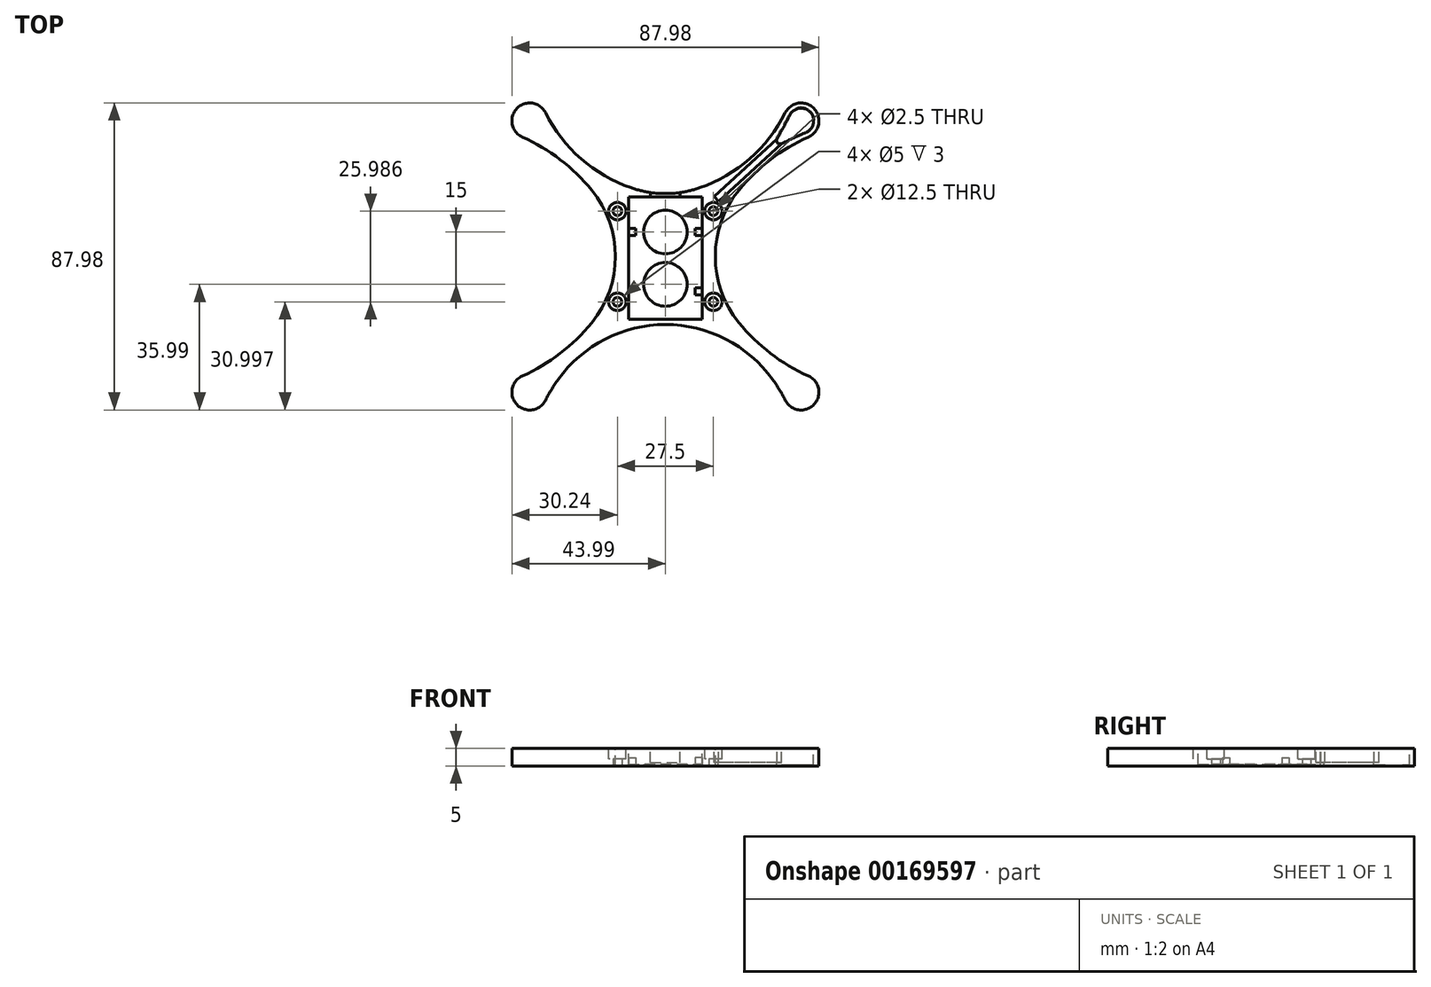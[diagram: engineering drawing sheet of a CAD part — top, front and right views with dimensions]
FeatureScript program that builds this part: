
annotation { "Feature Type Name" : "Feature", "Feature Type Description" : "" }
export const myFeature = defineFeature(function(context is Context, id is Id, definition is map)
    precondition{}
    {
        {
            var Q0;
            Q0=qCreatedBy(makeId("Top.planeOp"),FACE);
            var sketch = newSketch(context, id + "F0", { "sketchPlane" : qUnion([Q0])});
            skLineSegment(sketch, "E0.bottom", {"start": v(50, 50) * mm, "end": v(-50, 50) * mm, "construction": true});
            skLineSegment(sketch, "E0.top", {"start": v(50, -50) * mm, "end": v(-50, -50) * mm, "construction": true});
            skLineSegment(sketch, "E0.left", {"start": v(50, 50) * mm, "end": v(50, -50) * mm, "construction": true});
            skLineSegment(sketch, "E0.right", {"start": v(-50, 50) * mm, "end": v(-50, -50) * mm, "construction": true});
            skPoint(sketch, "E0.middle", {"position": v(0, 0) * mm});
            skSolve(sketch);
        }
        {
            var Q0;
            Q0=qCreatedBy(makeId("Top.planeOp"),FACE);
            var sketch = newSketch(context, id + "F1", { "sketchPlane" : qUnion([Q0])});
            skCircle(sketch, "E1", {"center": v(38.9, 38.9) * mm, "radius": 3.6 * mm, "construction": true});
            skLineSegment(sketch, "E2", {"start": v(0, 0) * mm, "end": v(65.42, 0) * mm, "construction": true});
            skLineSegment(sketch, "E3", {"start": v(0, 0) * mm, "end": v(0, 57) * mm, "construction": true});
            skLineSegment(sketch, "E4.bottom", {"start": v(11, 17.5) * mm, "end": v(-11, 17.5) * mm, "construction": true});
            skLineSegment(sketch, "E4.top", {"start": v(11, -17.5) * mm, "end": v(-11, -17.5) * mm, "construction": true});
            skLineSegment(sketch, "E4.left", {"start": v(11, 17.5) * mm, "end": v(11, -17.5) * mm, "construction": true});
            skLineSegment(sketch, "E4.right", {"start": v(-11, 17.5) * mm, "end": v(-11, -17.5) * mm, "construction": true});
            skPoint(sketch, "E4.middle", {"position": v(0, 0) * mm});
            skArc(sketch, "E5", {"start": v(40.98, 34.24) * mm, "mid": v(42.57, 42.42) * mm, "end": v(34.33, 41.17) * mm});
            skLineSegment(sketch, "E6", {"start": v(11, 17.5) * mm, "end": v(38.9, 38.9) * mm, "construction": true});
            skArc(sketch, "E7", {"start": v(40.98, 34.24) * mm, "mid": v(22.26, 20.39) * mm, "end": v(11, 0) * mm});
            skArc(sketch, "E8", {"start": v(0, 17.5) * mm, "mid": v(20.2, 24.92) * mm, "end": v(34.33, 41.17) * mm});
            skArc(sketch, "E9.MirrorCS", {"start": v(-40.98, 34.24) * mm, "mid": v(-42.57, 42.42) * mm, "end": v(-34.33, 41.17) * mm});
            skArc(sketch, "E10.MirrorCS", {"start": v(0, 17.5) * mm, "mid": v(-20.2, 24.92) * mm, "end": v(-34.33, 41.17) * mm});
            skArc(sketch, "E11.MirrorCS", {"start": v(-40.98, 34.24) * mm, "mid": v(-22.26, 20.39) * mm, "end": v(-11, 0) * mm});
            skArc(sketch, "E12.MirrorCS", {"start": v(40.98, -34.24) * mm, "mid": v(42.57, -42.42) * mm, "end": v(34.33, -41.17) * mm});
            skArc(sketch, "E13.MirrorCS", {"start": v(30.74, -35.24) * mm, "mid": v(32.66, -38.14) * mm, "end": v(34.33, -41.17) * mm});
            skArc(sketch, "E14.MirrorCS", {"start": v(40.98, -34.24) * mm, "mid": v(22.26, -20.39) * mm, "end": v(11, 0) * mm});
            skArc(sketch, "E15.MirrorCS", {"start": v(-40.98, -34.24) * mm, "mid": v(-42.57, -42.42) * mm, "end": v(-34.33, -41.17) * mm});
            skArc(sketch, "E16.MirrorCS", {"start": v(-30.74, -35.24) * mm, "mid": v(-32.66, -38.14) * mm, "end": v(-34.33, -41.17) * mm});
            skArc(sketch, "E17.MirrorCS", {"start": v(-40.98, -34.24) * mm, "mid": v(-22.26, -20.39) * mm, "end": v(-11, 0) * mm});
            skLineSegment(sketch, "E18", {"start": v(0, 0) * mm, "end": v(50, 50) * mm, "construction": true});
            skArc(sketch, "E19", {"start": v(30.74, -35.24) * mm, "mid": v(0, -19.5) * mm, "end": v(-30.74, -35.24) * mm});
            skPoint(sketch, "E20.orphan", {"position": v(0, -17.5) * mm});
            skSolve(sketch);
        }
        {
            var Q0;
            Q0=makeQuery(id+"F1.imprint","IMPRINT",FACE,{"disambiguationData":[TD([[makeQuery(id+"F1.imprint","IMPRINT",EDGE,{"derivedFrom":sQuery(id+"F1.wireOp",EDGE,"E5")}),1.0]])]});
            extrude(context, id + "F2", {"entities" : qUnion([Q0]), "depth" : 5 * mm});
        }
        {
            var Q0;
            Q0=makeQuery(id+"F2.opExtrude","CAP_FACE",FACE,{"disambiguationData":[OSD([sQuery(id+"F1.wireOp",EDGE,"E5"),sQuery(id+"F1.wireOp",EDGE,"E7"),sQuery(id+"F1.wireOp",EDGE,"E8"),sQuery(id+"F1.wireOp",EDGE,"E9.MirrorCS"),sQuery(id+"F1.wireOp",EDGE,"E10.MirrorCS"),sQuery(id+"F1.wireOp",EDGE,"E11.MirrorCS"),sQuery(id+"F1.wireOp",EDGE,"E12.MirrorCS"),sQuery(id+"F1.wireOp",EDGE,"E13.MirrorCS"),sQuery(id+"F1.wireOp",EDGE,"E14.MirrorCS"),sQuery(id+"F1.wireOp",EDGE,"E15.MirrorCS"),sQuery(id+"F1.wireOp",EDGE,"E16.MirrorCS"),sQuery(id+"F1.wireOp",EDGE,"E17.MirrorCS")])],"isStart":false});
            var sketch = newSketch(context, id + "F3", { "sketchPlane" : qUnion([Q0])});
            skArc(sketch, "E21", {"start": v(40.33, 35.6) * mm, "mid": v(41.51, 41.36) * mm, "end": v(35.69, 40.53) * mm});
            skArc(sketch, "E22", {"start": v(32.02, 33.75) * mm, "mid": v(32.16, 32.57) * mm, "end": v(33.33, 32.35) * mm});
            skArc(sketch, "E23", {"start": v(40.33, 35.6) * mm, "mid": v(36.81, 34.01) * mm, "end": v(33.33, 32.35) * mm});
            skLineSegment(sketch, "E24", {"start": v(32.89, 33.25) * mm, "end": v(38.9, 38.9) * mm, "construction": true});
            skArc(sketch, "E25.MirrorCS", {"start": v(35.69, 40.53) * mm, "mid": v(33.9, 37.12) * mm, "end": v(32.02, 33.75) * mm});
            skLineSegment(sketch, "E26", {"start": v(27.7, 25.78) * mm, "end": v(24.94, 28.7) * mm});
            skSolve(sketch);
        }
        {
            var Q0;
            Q0=makeQuery(id+"F3.imprint","IMPRINT",FACE,{"disambiguationData":[TD([[makeQuery(id+"F3.imprint","IMPRINT",EDGE,{"derivedFrom":sQuery(id+"F3.wireOp",EDGE,"E21")}),1.0]])]});
            extrude(context, id + "F4", {"entities" : qUnion([Q0]), "operationType" : NewBodyOperationType.REMOVE, "endBound" : BoundingType.THROUGH_ALL, "oppositeDirection" : true, "depth" : 25 * mm});
        }
        {
            var Q0;
            Q0=makeQuery(id+"F2.opExtrude","CAP_FACE",FACE,{"disambiguationData":[OSD([sQuery(id+"F1.wireOp",EDGE,"E5"),sQuery(id+"F1.wireOp",EDGE,"E7"),sQuery(id+"F1.wireOp",EDGE,"E8"),sQuery(id+"F1.wireOp",EDGE,"E9.MirrorCS"),sQuery(id+"F1.wireOp",EDGE,"E10.MirrorCS"),sQuery(id+"F1.wireOp",EDGE,"E11.MirrorCS"),sQuery(id+"F1.wireOp",EDGE,"E12.MirrorCS"),sQuery(id+"F1.wireOp",EDGE,"E13.MirrorCS"),sQuery(id+"F1.wireOp",EDGE,"E14.MirrorCS"),sQuery(id+"F1.wireOp",EDGE,"E15.MirrorCS"),sQuery(id+"F1.wireOp",EDGE,"E16.MirrorCS"),sQuery(id+"F1.wireOp",EDGE,"E17.MirrorCS"),sQuery(id+"F1.wireOp",EDGE,"E19")])],"isStart":false});
            var sketch = newSketch(context, id + "F5", { "sketchPlane" : qUnion([Q0])});
            skLineSegment(sketch, "E27", {"start": v(33.33, 32.35) * mm, "end": v(15.3, 15.76) * mm});
            skLineSegment(sketch, "E28", {"start": v(32.02, 33.75) * mm, "end": v(14, 17.17) * mm});
            skLineSegment(sketch, "E29", {"start": v(15.3, 15.76) * mm, "end": v(14, 17.17) * mm});
            skLineSegment(sketch, "E30", {"start": v(32.02, 33.75) * mm, "end": v(33.33, 32.35) * mm});
            skSolve(sketch);
        }
        {
            var Q0;
            Q0=makeQuery(id+"F5.imprint","IMPRINT",FACE,{"disambiguationData":[TD([[makeQuery(id+"F5.imprint","IMPRINT",EDGE,{"derivedFrom":sQuery(id+"F5.wireOp",EDGE,"E27")}),-1.0]])]});
            extrude(context, id + "F6", {"entities" : qUnion([Q0]), "operationType" : NewBodyOperationType.REMOVE, "oppositeDirection" : true, "depth" : 4 * mm});
        }
        {
            var Q0;
            Q0=makeQuery(id+"F2.opExtrude","SWEPT_EDGE",EDGE,{"disambiguationData":[OSD([sQuery(id+"F1.wireOp",EDGE,"E7"),sQuery(id+"F1.wireOp",EDGE,"E14.MirrorCS")])]});
            var Q1;
            Q1=makeQuery(id+"F2.opExtrude","SWEPT_EDGE",EDGE,{"disambiguationData":[OSD([sQuery(id+"F1.wireOp",EDGE,"E13.MirrorCS"),sQuery(id+"F1.wireOp",EDGE,"E16.MirrorCS")])]});
            var Q2;
            Q2=makeQuery(id+"F2.opExtrude","SWEPT_EDGE",EDGE,{"disambiguationData":[OSD([sQuery(id+"F1.wireOp",EDGE,"E11.MirrorCS"),sQuery(id+"F1.wireOp",EDGE,"E17.MirrorCS")])]});
            var Q3;
            Q3=makeQuery(id+"F2.opExtrude","SWEPT_EDGE",EDGE,{"disambiguationData":[OSD([sQuery(id+"F1.wireOp",EDGE,"E8"),sQuery(id+"F1.wireOp",EDGE,"E10.MirrorCS")])]});
            fillet(context, id + "F7", {"entities" : qUnion([Q0, Q1, Q2, Q3]), "radius" : 30 * mm, "tangentPropagation" : true, "allowEdgeOverflow" : false});
        }
        {
            var Q0;
            Q0=makeQuery(id+"F4.boolean.opBoolean","INTERSECT",EDGE,{"derivedFrom":[makeQuery(id+"F2.opExtrude","CAP_FACE",FACE,{"disambiguationData":[OSD([sQuery(id+"F1.wireOp",EDGE,"E5"),sQuery(id+"F1.wireOp",EDGE,"E7"),sQuery(id+"F1.wireOp",EDGE,"E8"),sQuery(id+"F1.wireOp",EDGE,"E9.MirrorCS"),sQuery(id+"F1.wireOp",EDGE,"E10.MirrorCS"),sQuery(id+"F1.wireOp",EDGE,"E11.MirrorCS"),sQuery(id+"F1.wireOp",EDGE,"E12.MirrorCS"),sQuery(id+"F1.wireOp",EDGE,"E13.MirrorCS"),sQuery(id+"F1.wireOp",EDGE,"E14.MirrorCS"),sQuery(id+"F1.wireOp",EDGE,"E15.MirrorCS"),sQuery(id+"F1.wireOp",EDGE,"E16.MirrorCS"),sQuery(id+"F1.wireOp",EDGE,"E17.MirrorCS")])],"isStart":true}),makeQuery(id+"F4.opExtrude","SWEPT_FACE",FACE,{"disambiguationData":[OSD([sQuery(id+"F3.wireOp",EDGE,"E21")])]})]});
            var Q1;
            Q1=makeQuery(id+"FYeeliCWMMzlBYI_1.1.F4.boolean.opBoolean","INTERSECT",EDGE,{"derivedFrom":[makeQuery(id+"F2.opExtrude","CAP_FACE",FACE,{"disambiguationData":[OSD([sQuery(id+"F1.wireOp",EDGE,"E5"),sQuery(id+"F1.wireOp",EDGE,"E7"),sQuery(id+"F1.wireOp",EDGE,"E8"),sQuery(id+"F1.wireOp",EDGE,"E9.MirrorCS"),sQuery(id+"F1.wireOp",EDGE,"E10.MirrorCS"),sQuery(id+"F1.wireOp",EDGE,"E11.MirrorCS"),sQuery(id+"F1.wireOp",EDGE,"E12.MirrorCS"),sQuery(id+"F1.wireOp",EDGE,"E13.MirrorCS"),sQuery(id+"F1.wireOp",EDGE,"E14.MirrorCS"),sQuery(id+"F1.wireOp",EDGE,"E15.MirrorCS"),sQuery(id+"F1.wireOp",EDGE,"E16.MirrorCS"),sQuery(id+"F1.wireOp",EDGE,"E17.MirrorCS")])],"isStart":true}),makeQuery(id+"FYeeliCWMMzlBYI_1.1.F4.opExtrude","SWEPT_FACE",FACE,{"disambiguationData":[OSD([sQuery(id+"F3.wireOp",EDGE,"E21")])]})]});
            var Q2;
            Q2=makeQuery(id+"FTFssc0xpSEtFVF_1.1.FYeeliCWMMzlBYI_1.1.F4.boolean.opBoolean","INTERSECT",EDGE,{"derivedFrom":[makeQuery(id+"F2.opExtrude","CAP_FACE",FACE,{"disambiguationData":[OSD([sQuery(id+"F1.wireOp",EDGE,"E5"),sQuery(id+"F1.wireOp",EDGE,"E7"),sQuery(id+"F1.wireOp",EDGE,"E8"),sQuery(id+"F1.wireOp",EDGE,"E9.MirrorCS"),sQuery(id+"F1.wireOp",EDGE,"E10.MirrorCS"),sQuery(id+"F1.wireOp",EDGE,"E11.MirrorCS"),sQuery(id+"F1.wireOp",EDGE,"E12.MirrorCS"),sQuery(id+"F1.wireOp",EDGE,"E13.MirrorCS"),sQuery(id+"F1.wireOp",EDGE,"E14.MirrorCS"),sQuery(id+"F1.wireOp",EDGE,"E15.MirrorCS"),sQuery(id+"F1.wireOp",EDGE,"E16.MirrorCS"),sQuery(id+"F1.wireOp",EDGE,"E17.MirrorCS")])],"isStart":true}),makeQuery(id+"FTFssc0xpSEtFVF_1.1.FYeeliCWMMzlBYI_1.1.F4.opExtrude","SWEPT_FACE",FACE,{"disambiguationData":[OSD([sQuery(id+"F3.wireOp",EDGE,"E21")])]})]});
            var Q3;
            Q3=makeQuery(id+"FTFssc0xpSEtFVF_1.1.F4.boolean.opBoolean","INTERSECT",EDGE,{"derivedFrom":[makeQuery(id+"F2.opExtrude","CAP_FACE",FACE,{"disambiguationData":[OSD([sQuery(id+"F1.wireOp",EDGE,"E5"),sQuery(id+"F1.wireOp",EDGE,"E7"),sQuery(id+"F1.wireOp",EDGE,"E8"),sQuery(id+"F1.wireOp",EDGE,"E9.MirrorCS"),sQuery(id+"F1.wireOp",EDGE,"E10.MirrorCS"),sQuery(id+"F1.wireOp",EDGE,"E11.MirrorCS"),sQuery(id+"F1.wireOp",EDGE,"E12.MirrorCS"),sQuery(id+"F1.wireOp",EDGE,"E13.MirrorCS"),sQuery(id+"F1.wireOp",EDGE,"E14.MirrorCS"),sQuery(id+"F1.wireOp",EDGE,"E15.MirrorCS"),sQuery(id+"F1.wireOp",EDGE,"E16.MirrorCS"),sQuery(id+"F1.wireOp",EDGE,"E17.MirrorCS")])],"isStart":true}),makeQuery(id+"FTFssc0xpSEtFVF_1.1.F4.opExtrude","SWEPT_FACE",FACE,{"disambiguationData":[OSD([sQuery(id+"F3.wireOp",EDGE,"6V2njJEu-L4nl-PxpZ-iP1S-ceyWdav9gjuh")])]})]});
            chamfer(context, id + "F8", {"entities" : qUnion([Q0, Q1, Q2, Q3]), "width" : .3 * mm, "tangentPropagation" : true});
        }
        {
            var Q0;
            Q0=makeQuery(id+"F2.opExtrude","CAP_FACE",FACE,{"disambiguationData":[OSD([sQuery(id+"F1.wireOp",EDGE,"E5"),sQuery(id+"F1.wireOp",EDGE,"E7"),sQuery(id+"F1.wireOp",EDGE,"E8"),sQuery(id+"F1.wireOp",EDGE,"E9.MirrorCS"),sQuery(id+"F1.wireOp",EDGE,"E10.MirrorCS"),sQuery(id+"F1.wireOp",EDGE,"E11.MirrorCS"),sQuery(id+"F1.wireOp",EDGE,"E12.MirrorCS"),sQuery(id+"F1.wireOp",EDGE,"E13.MirrorCS"),sQuery(id+"F1.wireOp",EDGE,"E14.MirrorCS"),sQuery(id+"F1.wireOp",EDGE,"E15.MirrorCS"),sQuery(id+"F1.wireOp",EDGE,"E16.MirrorCS"),sQuery(id+"F1.wireOp",EDGE,"E17.MirrorCS")])],"isStart":false});
            var sketch = newSketch(context, id + "F9", { "sketchPlane" : qUnion([Q0])});
            skLineSegment(sketch, "E31.bottom", {"start": v(-10.5, -18) * mm, "end": v(10.5, -18) * mm});
            skLineSegment(sketch, "E31.top", {"start": v(-10.5, 17) * mm, "end": v(10.5, 17) * mm});
            skLineSegment(sketch, "E31.left", {"start": v(-10.5, -18) * mm, "end": v(-10.5, 17) * mm});
            skLineSegment(sketch, "E31.right", {"start": v(10.5, -18) * mm, "end": v(10.5, 17) * mm});
            skSolve(sketch);
        }
        {
            var Q0;
            Q0 = qSketchRegion(id + "F9", true);
            extrude(context, id + "F10", {"entities" : qUnion([Q0]), "operationType" : NewBodyOperationType.REMOVE, "oppositeDirection" : true, "depth" : 4.5 * mm});
        }
        {
            var Q0;
            Q0=makeQuery(id+"F10.boolean.opBoolean","COPY",FACE,{"derivedFrom":makeQuery(id+"F10.opExtrude","CAP_FACE",FACE,{"disambiguationData":[OSD([sQuery(id+"F9.wireOp",EDGE,"E31.bottom"),sQuery(id+"F9.wireOp",EDGE,"E31.top"),sQuery(id+"F9.wireOp",EDGE,"E31.left"),sQuery(id+"F9.wireOp",EDGE,"E31.right")])],"isStart":false})});
            var sketch = newSketch(context, id + "F11", { "sketchPlane" : qUnion([Q0])});
            skLineSegment(sketch, "E32.bottom", {"start": v(-10.5, 6) * mm, "end": v(-8.5, 6) * mm});
            skLineSegment(sketch, "E32.top", {"start": v(-10.5, 8) * mm, "end": v(-8.5, 8) * mm});
            skLineSegment(sketch, "E32.left", {"start": v(-10.5, 8) * mm, "end": v(-10.5, 6) * mm});
            skLineSegment(sketch, "E32.right", {"start": v(-8.5, 8) * mm, "end": v(-8.5, 6) * mm});
            skLineSegment(sketch, "E33.MirrorCS", {"start": v(10.5, 6) * mm, "end": v(8.5, 6) * mm});
            skLineSegment(sketch, "E34.MirrorCS", {"start": v(8.5, 8) * mm, "end": v(8.5, 6) * mm});
            skLineSegment(sketch, "E35.MirrorCS", {"start": v(10.5, 8) * mm, "end": v(8.5, 8) * mm});
            skLineSegment(sketch, "E36.MirrorCS", {"start": v(10.5, 8) * mm, "end": v(10.5, 6) * mm});
            skLineSegment(sketch, "E37.bottom", {"start": v(10.5, -11) * mm, "end": v(8.5, -11) * mm});
            skLineSegment(sketch, "E37.top", {"start": v(10.5, -9) * mm, "end": v(8.5, -9) * mm});
            skLineSegment(sketch, "E37.left", {"start": v(10.5, -11) * mm, "end": v(10.5, -9) * mm});
            skLineSegment(sketch, "E37.right", {"start": v(8.5, -11) * mm, "end": v(8.5, -9) * mm});
            skSolve(sketch);
        }
        {
            var Q0;
            Q0 = qSketchRegion(id + "F11", true);
            extrude(context, id + "F12", {"entities" : qUnion([Q0]), "operationType" : NewBodyOperationType.ADD, "depth" : 1.95 * mm});
        }
        {
            var Q0;
            Q0=qCreatedBy(makeId("Top.planeOp"),FACE);
            var sketch = newSketch(context, id + "F13", { "sketchPlane" : qUnion([Q0])});
            skCircle(sketch, "E38", {"center": v(-13.75, 13) * mm, "radius": 1.25 * mm});
            skCircle(sketch, "E39.MirrorC", {"center": v(13.75, 13) * mm, "radius": 1.25 * mm});
            skCircle(sketch, "E40.MirrorC", {"center": v(13.75, -13) * mm, "radius": 1.25 * mm});
            skCircle(sketch, "E41.MirrorC", {"center": v(-13.75, -13) * mm, "radius": 1.25 * mm});
            skCircle(sketch, "E42", {"center": v(0, 7) * mm, "radius": 6.25 * mm});
            skCircle(sketch, "E43", {"center": v(0, -8) * mm, "radius": 6.25 * mm});
            skSolve(sketch);
        }
        {
            var Q0;
            Q0 = qSketchRegion(id + "F13", true);
            extrude(context, id + "F14", {"entities" : qUnion([Q0]), "operationType" : NewBodyOperationType.REMOVE, "endBound" : BoundingType.THROUGH_ALL, "depth" : 25 * mm});
        }
        {
            var Q0;
            Q0=makeQuery(id+"F2.opExtrude","CAP_FACE",FACE,{"disambiguationData":[OSD([sQuery(id+"F1.wireOp",EDGE,"E5"),sQuery(id+"F1.wireOp",EDGE,"E7"),sQuery(id+"F1.wireOp",EDGE,"E8"),sQuery(id+"F1.wireOp",EDGE,"E9.MirrorCS"),sQuery(id+"F1.wireOp",EDGE,"E10.MirrorCS"),sQuery(id+"F1.wireOp",EDGE,"E11.MirrorCS"),sQuery(id+"F1.wireOp",EDGE,"E12.MirrorCS"),sQuery(id+"F1.wireOp",EDGE,"E13.MirrorCS"),sQuery(id+"F1.wireOp",EDGE,"E14.MirrorCS"),sQuery(id+"F1.wireOp",EDGE,"E15.MirrorCS"),sQuery(id+"F1.wireOp",EDGE,"E16.MirrorCS"),sQuery(id+"F1.wireOp",EDGE,"E17.MirrorCS"),sQuery(id+"F1.wireOp",EDGE,"E19")])],"isStart":false});
            var sketch = newSketch(context, id + "F15", { "sketchPlane" : qUnion([Q0])});
            skLineSegment(sketch, "E44.bottom", {"start": v(-4.25, 17) * mm, "end": v(4.25, 17) * mm});
            skLineSegment(sketch, "E44.top", {"start": v(-4.25, 22) * mm, "end": v(4.25, 22) * mm});
            skLineSegment(sketch, "E44.left", {"start": v(-4.25, 17) * mm, "end": v(-4.25, 22) * mm});
            skLineSegment(sketch, "E44.right", {"start": v(4.25, 17) * mm, "end": v(4.25, 22) * mm});
            skSolve(sketch);
        }
        {
            var Q0;
            {var subQ0=sQuery(id+"F15.wireOp",EDGE,"E44.top");Q0=makeQuery(id+"F15.imprint","IMPRINT",FACE,{"disambiguationData":[TD([[makeQuery(id+"F15.imprint","IMPRINT",EDGE,{"derivedFrom":subQ0}),-1.0]])]});}
            var Q1;
            {var subQ0=sQuery(id+"F15.wireOp",EDGE,"E44.bottom");Q1=makeQuery(id+"F15.imprint","IMPRINT",FACE,{"disambiguationData":[TD([[makeQuery(id+"F15.imprint","IMPRINT",EDGE,{"derivedFrom":subQ0}),1.0]])]});}
            extrude(context, id + "F16", {"entities" : qUnion([Q0, Q1]), "operationType" : NewBodyOperationType.REMOVE, "oppositeDirection" : true, "depth" : 4 * mm});
        }
        {
            var Q0;
            Q0=makeQuery(id+"F2.opExtrude","CAP_FACE",FACE,{"disambiguationData":[OSD([sQuery(id+"F1.wireOp",EDGE,"E5"),sQuery(id+"F1.wireOp",EDGE,"E7"),sQuery(id+"F1.wireOp",EDGE,"E8"),sQuery(id+"F1.wireOp",EDGE,"E9.MirrorCS"),sQuery(id+"F1.wireOp",EDGE,"E10.MirrorCS"),sQuery(id+"F1.wireOp",EDGE,"E11.MirrorCS"),sQuery(id+"F1.wireOp",EDGE,"E12.MirrorCS"),sQuery(id+"F1.wireOp",EDGE,"E13.MirrorCS"),sQuery(id+"F1.wireOp",EDGE,"E14.MirrorCS"),sQuery(id+"F1.wireOp",EDGE,"E15.MirrorCS"),sQuery(id+"F1.wireOp",EDGE,"E16.MirrorCS"),sQuery(id+"F1.wireOp",EDGE,"E17.MirrorCS"),sQuery(id+"F1.wireOp",EDGE,"E19")])],"isStart":false});
            var sketch = newSketch(context, id + "F17", { "sketchPlane" : qUnion([Q0])});
            skCircle(sketch, "E45", {"center": v(13.75, -13) * mm, "radius": 2.5 * mm});
            skCircle(sketch, "E46", {"center": v(-13.75, -13) * mm, "radius": 2.5 * mm});
            skCircle(sketch, "E47", {"center": v(-13.75, 13) * mm, "radius": 2.5 * mm});
            skCircle(sketch, "E48", {"center": v(13.75, 13) * mm, "radius": 2.5 * mm});
            skSolve(sketch);
        }
        {
            var Q0;
            Q0=makeQuery(id+"F17.imprint","IMPRINT",FACE,{"disambiguationData":[TD([[makeQuery(id+"F17.imprint","IMPRINT",EDGE,{"derivedFrom":sQuery(id+"F17.wireOp",EDGE,"E45")}),1.0]])]});
            var Q1;
            Q1=makeQuery(id+"F17.imprint","IMPRINT",FACE,{"disambiguationData":[TD([[makeQuery(id+"F17.imprint","IMPRINT",EDGE,{"derivedFrom":sQuery(id+"F17.wireOp",EDGE,"E46")}),1.0]])]});
            var Q2;
            Q2=makeQuery(id+"F17.imprint","IMPRINT",FACE,{"disambiguationData":[TD([[makeQuery(id+"F17.imprint","IMPRINT",EDGE,{"derivedFrom":sQuery(id+"F17.wireOp",EDGE,"E48")}),1.0]])]});
            var Q3;
            Q3=makeQuery(id+"F17.imprint","IMPRINT",FACE,{"disambiguationData":[TD([[makeQuery(id+"F17.imprint","IMPRINT",EDGE,{"derivedFrom":sQuery(id+"F17.wireOp",EDGE,"E47")}),1.0]])]});
            extrude(context, id + "F18", {"entities" : qUnion([Q0, Q1, Q2, Q3]), "operationType" : NewBodyOperationType.REMOVE, "oppositeDirection" : true, "depth" : 3 * mm});
        }
    });
